# Revit family: PA_Арматура трубопроводов [клапан термостатический угловой, VT.033.N]1 - VALTEC
name_source: partatom
category: Арматура трубопроводов
revit_build: Autodesk Revit 2018 (Build: 20180423_1000(x64)
units: mm (PartAtom-declared; Revit-internal decimal feet)

## family parameters
Всегда вертикально = Да
На основе рабочей плоскости = Нет
Общий = Нет
При загрузке вырезать с полостями = Нет
Размер круглого соединителя = Использовать диаметр
Тип детали = Вставляется

## types (1)
- VT.033.N
    1!!!НЕ ИЗМЕНЯТЬ!!! = VT.1000.0.0
    10!!!НЕ ИЗМЕНЯТЬ!!! = VT.TE3041.A.024
    11!!!НЕ ИЗМЕНЯТЬ!!! = VT.TE3042.0.024
    12!!!НЕ ИЗМЕНЯТЬ!!! = VT.TE3042.0.220
    13!!!НЕ ИЗМЕНЯТЬ!!! = VT.TE3042.A.220
    14!!!НЕ ИЗМЕНЯТЬ!!! = Колпачок
    2!!!НЕ ИЗМЕНЯТЬ!!! = VT.1500.0.0
    3!!!НЕ ИЗМЕНЯТЬ!!! = VT.3000.0.0
    4!!!НЕ ИЗМЕНЯТЬ!!! = VT.5000.0.0
    5!!!НЕ ИЗМЕНЯТЬ!!! = VT.5010.0.0
    6!!!НЕ ИЗМЕНЯТЬ!!! = VT.AS1000
    7!!!НЕ ИЗМЕНЯТЬ!!! = VT.TE3040.0.220
    8!!!НЕ ИЗМЕНЯТЬ!!! = VT.TE3040.A.220
    9!!!НЕ ИЗМЕНЯТЬ!!! = VT.TE3041.0.024
    ADSK_URL документации изделия = https://valtec.ru
    ADSK_URL страницы изделия = https://valtec.ru
    ADSK_Материал = Сталь, нержавеющая - VALTEC
    ME_1!!!НЕ ИЗМЕНЯТЬ!!! = ME_Оборудование [головка термостатическая твердотельная, VT.1000.0] - VALTEC
    ME_10!!!НЕ ИЗМЕНЯТЬ!!! = ME_Оборудование [сервопривод электрический, VT.TE3041.A.024] - VALTEC
    ME_11!!!НЕ ИЗМЕНЯТЬ!!! = ME_Оборудование [сервопривод электрический, VT.TE3042.0.024] - VALTEC
    ME_12!!!НЕ ИЗМЕНЯТЬ!!! = ME_Оборудование [сервопривод электрический, VT.TE3042.0.220] - VALTEC
    ME_13!!!НЕ ИЗМЕНЯТЬ!!! = ME_Оборудование [сервопривод электрический, VT.TE3042.A.220] - VALTEC
    ME_14!!!НЕ ИЗМЕНЯТЬ!!! = ME_Оборудование [колпачек] - VALTEC
    ME_2!!!НЕ ИЗМЕНЯТЬ!!! = ME_Оборудование [головка термостатическая жидкостная, VT.1500.0] - VALTEC
    ME_3!!!НЕ ИЗМЕНЯТЬ!!! = ME_Оборудование [головка термостатическая жидкостная, VT.3000.0] - VALTEC
    ME_4!!!НЕ ИЗМЕНЯТЬ!!! = ME_Оборудование [головка термостатическая жидкостная, VT.5000.0] - VALTEC
    ME_5!!!НЕ ИЗМЕНЯТЬ!!! = ME_Оборудование [головка термостатическая жидкостная, VT.5010.0] - VALTEC
    ME_6!!!НЕ ИЗМЕНЯТЬ!!! = ME_Оборудование [cервопривод EQUICALOR, VT.AS1000] - VALTEC
    ME_7!!!НЕ ИЗМЕНЯТЬ!!! = ME_Оборудование [сервопривод электрический, VT.TE3040.0.220] - VALTEC
    ME_8!!!НЕ ИЗМЕНЯТЬ!!! = ME_Оборудование [сервопривод электрический, VT.TE3040.A.220] - VALTEC
    ME_9!!!НЕ ИЗМЕНЯТЬ!!! = ME_Оборудование [сервопривод электрический, VT.TE3041.0.024] - VALTEC
    MM_1!!!НЕ ИЗМЕНЯТЬ!!! = MM_Обобщенные модели [головка термостатическая твердотельная, VT.1000.0] - VALTEC : VT.1000.0
    MM_2!!!НЕ ИЗМЕНЯТЬ!!! = MM_Обобщенные модели [головка термостатическая жидкостная, VT.1500.0] - VALTEC : VT.1500.0
    MM_3!!!НЕ ИЗМЕНЯТЬ!!! = MM_Обобщенные модели [головка термостатическая жидкостная, VT.3000.0] - VALTEC : VT.3000.0
    MM_4!!!НЕ ИЗМЕНЯТЬ!!! = MM_Обобщенные модели [головка термостатическая жидкостная, VT.5000.0] - VALTEC : VT.5000.0 - VT.5010.0
    MM_5!!!НЕ ИЗМЕНЯТЬ!!! = MM_Обобщенные модели [cервопривод EQUICALOR, VT.AS1000] - VALTEC : VT.AS1000
    MM_6!!!НЕ ИЗМЕНЯТЬ!!! = MM_Обобщенные модели [сервопривод электрический, VT.TE3040] - VALTEC : VT.TE3040
    MM_7!!!НЕ ИЗМЕНЯТЬ!!! = MM_Обобщенные модели [сервопривод электрический, VT.TE3042] - VALTEC : VT.TE3042.0
    MM_8!!!НЕ ИЗМЕНЯТЬ!!! = MM_Обобщенные модели [колпачок, VT.033.N] - VALTEC : VT.TE3042.0
    URL = https://valtec.ru
    Изготовитель = VALTEC
    Материал доп.1 = Черный - VALTEC
    Таблица 1 = PA_Арматура трубопроводов [клапан термостатический угловой, VT.033.N] - VALTEC - Таблица 1
    Таблица 2 = PA_Арматура трубопроводов [клапан термостатический угловой, VT.033.N] - VALTEC - Таблица 2
